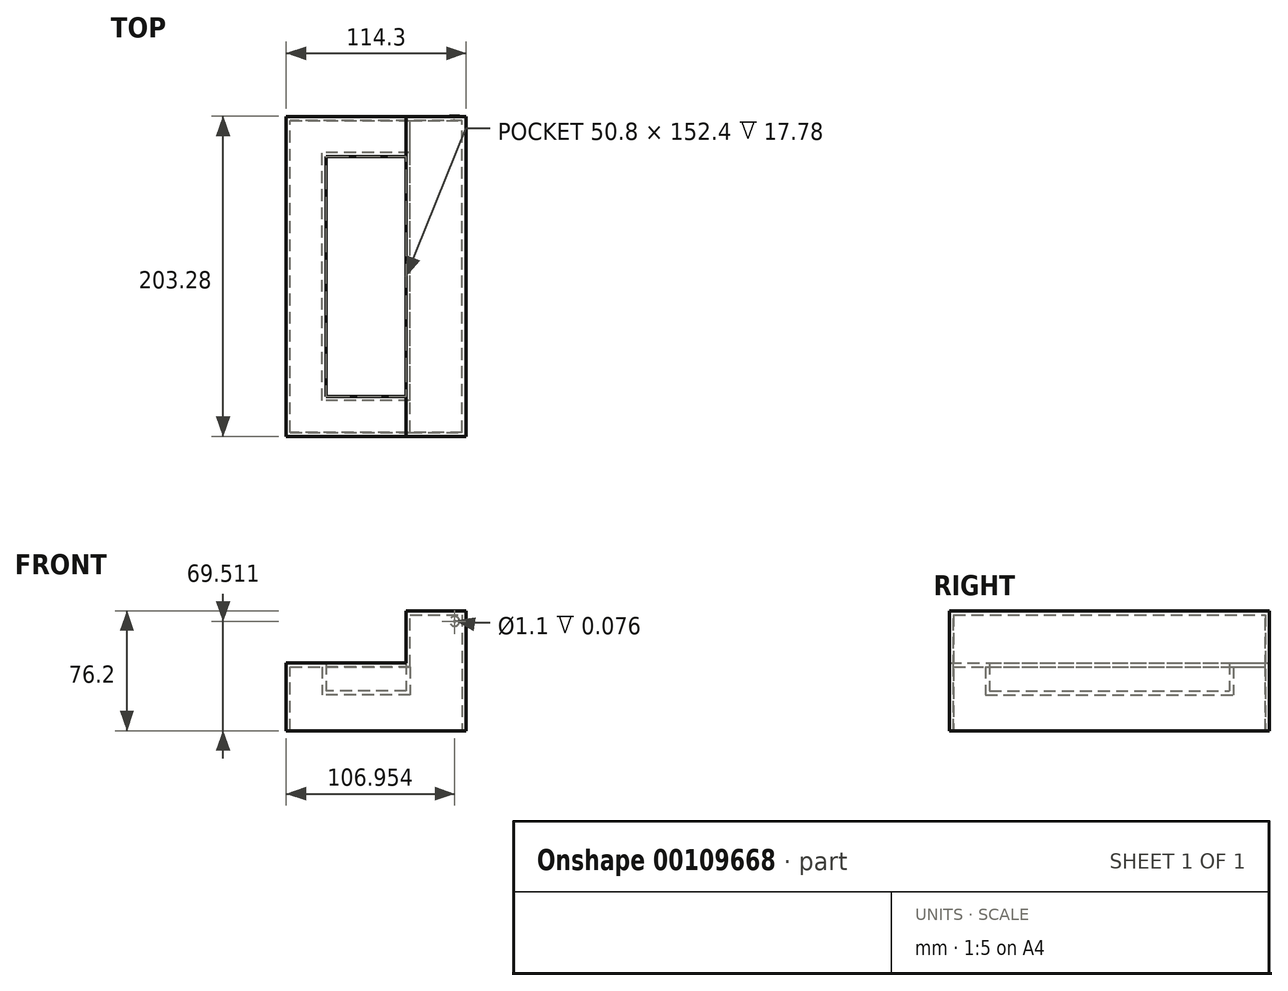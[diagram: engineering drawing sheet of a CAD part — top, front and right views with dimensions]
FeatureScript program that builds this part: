
annotation { "Feature Type Name" : "Feature", "Feature Type Description" : "" }
export const myFeature = defineFeature(function(context is Context, id is Id, definition is map)
    precondition{}
    {
        {
            var Q0;
            Q0=qCreatedBy(makeId("Front.planeOp"),FACE);
            var sketch = newSketch(context, id + "F0", { "sketchPlane" : qUnion([Q0])});
            skLineSegment(sketch, "E0", {"start": v(-17.88, -41.6) * mm, "end": v(7.52, -41.6) * mm});
            skLineSegment(sketch, "E1", {"start": v(7.52, -41.6) * mm, "end": v(7.52, -59.39) * mm});
            skLineSegment(sketch, "E2", {"start": v(7.52, -59.39) * mm, "end": v(58.32, -59.39) * mm});
            skLineSegment(sketch, "E3", {"start": v(58.32, -59.39) * mm, "end": v(58.32, -8.59) * mm});
            skLineSegment(sketch, "E4", {"start": v(58.32, -8.59) * mm, "end": v(96.42, -8.59) * mm});
            skLineSegment(sketch, "E5", {"start": v(96.42, -8.59) * mm, "end": v(96.42, -84.79) * mm});
            skLineSegment(sketch, "E6", {"start": v(96.42, -84.79) * mm, "end": v(-17.88, -84.79) * mm});
            skLineSegment(sketch, "E7", {"start": v(-17.88, -84.79) * mm, "end": v(-17.88, -41.6) * mm});
            skSolve(sketch);
        }
        {
            var Q0;
            Q0=makeQuery(id+"F0.imprint","IMPRINT",FACE,{"disambiguationData":[TD([[makeQuery(id+"F0.imprint","IMPRINT",EDGE,{"derivedFrom":sQuery(id+"F0.wireOp",EDGE,"E0")}),-1.0]])]});
            extrude(context, id + "F1", {"entities" : qUnion([Q0]), "depth" : 203.2 * mm});
        }
        {
            var Q0;
            Q0=makeQuery(id+"F1.opExtrude","SWEPT_FACE",FACE,{"disambiguationData":[OSD([sQuery(id+"F0.wireOp",EDGE,"E1")])]});
            var sketch = newSketch(context, id + "F2", { "sketchPlane" : qUnion([Q0])});
            skLineSegment(sketch, "E8.bottom", {"start": v(-203.2, -41.6) * mm, "end": v(-177.8, -41.6) * mm});
            skLineSegment(sketch, "E8.top", {"start": v(-203.2, -59.39) * mm, "end": v(-177.8, -59.39) * mm});
            skLineSegment(sketch, "E8.left", {"start": v(-203.2, -41.6) * mm, "end": v(-203.2, -59.39) * mm});
            skLineSegment(sketch, "E8.right", {"start": v(-177.8, -41.6) * mm, "end": v(-177.8, -59.39) * mm});
            skSolve(sketch);
        }
        {
            var Q0;
            Q0=makeQuery(id+"F2.imprint","IMPRINT",FACE,{"disambiguationData":[TD([[makeQuery(id+"F2.imprint","IMPRINT",EDGE,{"derivedFrom":sQuery(id+"F2.wireOp",EDGE,"E8.bottom")}),-1.0]])]});
            extrude(context, id + "F3", {"entities" : qUnion([Q0]), "operationType" : NewBodyOperationType.ADD, "depth" : 50.8 * mm});
        }
        {
            var Q0;
            Q0=makeQuery(id+"F1.opExtrude","SWEPT_FACE",FACE,{"disambiguationData":[OSD([sQuery(id+"F0.wireOp",EDGE,"E1")])]});
            var sketch = newSketch(context, id + "F4", { "sketchPlane" : qUnion([Q0])});
            skLineSegment(sketch, "E9.bottom", {"start": v(0, -41.6) * mm, "end": v(-25.4, -41.6) * mm});
            skLineSegment(sketch, "E9.top", {"start": v(0, -59.39) * mm, "end": v(-25.4, -59.39) * mm});
            skLineSegment(sketch, "E9.left", {"start": v(0, -41.6) * mm, "end": v(0, -59.39) * mm});
            skLineSegment(sketch, "E9.right", {"start": v(-25.4, -41.6) * mm, "end": v(-25.4, -59.39) * mm});
            skSolve(sketch);
        }
        {
            var Q0;
            Q0=makeQuery(id+"F4.imprint","IMPRINT",FACE,{"disambiguationData":[TD([[makeQuery(id+"F4.imprint","IMPRINT",EDGE,{"derivedFrom":sQuery(id+"F4.wireOp",EDGE,"E9.bottom")}),-1.0]])]});
            extrude(context, id + "F5", {"entities" : qUnion([Q0]), "operationType" : NewBodyOperationType.ADD, "depth" : 50.8 * mm});
        }
        {
            var Q0;
            Q0=makeQuery(id+"F3.boolean.opBoolean","MERGE",FACE,{"derivedFrom":[makeQuery(id+"F1.opExtrude","CAP_FACE",FACE,{"disambiguationData":[OSD([sQuery(id+"F0.wireOp",EDGE,"E0"),sQuery(id+"F0.wireOp",EDGE,"E1"),sQuery(id+"F0.wireOp",EDGE,"E2"),sQuery(id+"F0.wireOp",EDGE,"E3"),sQuery(id+"F0.wireOp",EDGE,"E4"),sQuery(id+"F0.wireOp",EDGE,"E5"),sQuery(id+"F0.wireOp",EDGE,"E6"),sQuery(id+"F0.wireOp",EDGE,"E7")])],"isStart":false}),makeQuery(id+"F3.opExtrude","SWEPT_FACE",FACE,{"disambiguationData":[OSD([sQuery(id+"F2.wireOp",EDGE,"E8.left")])]})]});
            var sketch = newSketch(context, id + "F6", { "sketchPlane" : qUnion([Q0])});
            skCircle(sketch, "E10", {"center": v(2.53, -60.02) * mm, "radius": 8.97 * mm});
            skCircle(sketch, "E11", {"center": v(2.53, -60.02) * mm, "radius": 6.38 * mm});
            skCircle(sketch, "E12", {"center": v(2.53, -60.02) * mm, "radius": 3.86 * mm});
            skCircle(sketch, "E13", {"center": v(46.1, -54.58) * mm, "radius": 12.1 * mm});
            skCircle(sketch, "E14", {"center": v(46.1, -54.58) * mm, "radius": 8.06 * mm});
            skCircle(sketch, "E15", {"center": v(46.1, -54.58) * mm, "radius": 4.73 * mm});
            skCircle(sketch, "E16", {"center": v(25.1, -66.44) * mm, "radius": 7.01 * mm});
            skCircle(sketch, "E17", {"center": v(25.1, -66.44) * mm, "radius": 5.22 * mm});
            skCircle(sketch, "E18", {"center": v(25.1, -66.44) * mm, "radius": 2.9 * mm});
            skCircle(sketch, "E19", {"center": v(73.33, -30.85) * mm, "radius": 11.18 * mm});
            skCircle(sketch, "E20", {"center": v(73.33, -30.85) * mm, "radius": 8.9 * mm});
            skCircle(sketch, "E21", {"center": v(73.33, -30.85) * mm, "radius": 5.31 * mm});
            skCircle(sketch, "E22", {"center": v(76.83, -56.72) * mm, "radius": 10.12 * mm});
            skCircle(sketch, "E23", {"center": v(76.83, -56.72) * mm, "radius": 6.65 * mm});
            skCircle(sketch, "E24", {"center": v(76.83, -56.72) * mm, "radius": 3.76 * mm});
            skCircle(sketch, "E25", {"center": v(89.09, -15.48) * mm, "radius": 6.23 * mm});
            skCircle(sketch, "E26", {"center": v(89.09, -15.48) * mm, "radius": 4.92 * mm});
            skCircle(sketch, "E27", {"center": v(89.09, -15.48) * mm, "radius": 2.92 * mm});
            skCircle(sketch, "E28", {"center": v(57.58, -75.78) * mm, "radius": 6.65 * mm});
            skCircle(sketch, "E29", {"center": v(57.58, -75.78) * mm, "radius": 4.44 * mm});
            skCircle(sketch, "E30", {"center": v(57.58, -75.78) * mm, "radius": 2.27 * mm});
            skCircle(sketch, "E31", {"center": v(84.8, -75.59) * mm, "radius": 6.4 * mm});
            skCircle(sketch, "E32", {"center": v(84.8, -75.59) * mm, "radius": 4.68 * mm});
            skCircle(sketch, "E33", {"center": v(84.8, -75.59) * mm, "radius": 2.79 * mm});
            skCircle(sketch, "E34", {"center": v(-8.56, -74.8) * mm, "radius": 6.24 * mm});
            skCircle(sketch, "E35", {"center": v(-8.56, -74.8) * mm, "radius": 4.81 * mm});
            skCircle(sketch, "E36", {"center": v(-8.56, -74.8) * mm, "radius": 2.79 * mm});
            skCircle(sketch, "E37", {"center": v(-11.48, -47.19) * mm, "radius": 5.17 * mm});
            skCircle(sketch, "E38", {"center": v(-11.48, -47.19) * mm, "radius": 3.08 * mm});
            skCircle(sketch, "E39", {"center": v(-11.48, -47.19) * mm, "radius": 1.84 * mm});
            skCircle(sketch, "E40", {"center": v(16.92, -50.5) * mm, "radius": 6.14 * mm});
            skCircle(sketch, "E41", {"center": v(16.92, -50.5) * mm, "radius": 4.2 * mm});
            skCircle(sketch, "E42", {"center": v(16.92, -50.5) * mm, "radius": 2.65 * mm});
            skCircle(sketch, "E43", {"center": v(9.72, -76.17) * mm, "radius": 6.72 * mm});
            skCircle(sketch, "E44", {"center": v(9.72, -76.17) * mm, "radius": 5.15 * mm});
            skCircle(sketch, "E45", {"center": v(9.72, -76.17) * mm, "radius": 3.45 * mm});
            skCircle(sketch, "E46", {"center": v(35.98, -76.75) * mm, "radius": 3.02 * mm});
            skCircle(sketch, "E47", {"center": v(35.98, -76.75) * mm, "radius": 1.74 * mm});
            skCircle(sketch, "E48", {"center": v(35.98, -76.75) * mm, "radius": 4.77 * mm});
            skSolve(sketch);
        }
        {
            var Q0;
            Q0=makeQuery(id+"F1.opExtrude","SWEPT_FACE",FACE,{"disambiguationData":[OSD([sQuery(id+"F0.wireOp",EDGE,"E7")])]});
            var sketch = newSketch(context, id + "F7", { "sketchPlane" : qUnion([Q0])});
            skCircle(sketch, "E49", {"center": v(16.84, -58.1) * mm, "radius": 14.47 * mm});
            skCircle(sketch, "E50", {"center": v(16.84, -58.1) * mm, "radius": 9.9 * mm});
            skCircle(sketch, "E51", {"center": v(16.84, -58.1) * mm, "radius": 4.92 * mm});
            skCircle(sketch, "E52", {"center": v(67.39, -64.14) * mm, "radius": 8.57 * mm});
            skCircle(sketch, "E53", {"center": v(67.39, -64.14) * mm, "radius": 4.72 * mm});
            skCircle(sketch, "E54", {"center": v(67.39, -64.14) * mm, "radius": 2.75 * mm});
            skCircle(sketch, "E55", {"center": v(42.18, -76.46) * mm, "radius": 6.39 * mm});
            skCircle(sketch, "E56", {"center": v(42.18, -76.46) * mm, "radius": 4.32 * mm});
            skCircle(sketch, "E57", {"center": v(42.18, -76.46) * mm, "radius": 2.37 * mm});
            skCircle(sketch, "E58", {"center": v(136.66, -60.8) * mm, "radius": 18.27 * mm});
            skCircle(sketch, "E59", {"center": v(136.66, -60.8) * mm, "radius": 13.93 * mm});
            skCircle(sketch, "E60", {"center": v(136.66, -60.8) * mm, "radius": 6.71 * mm});
            skCircle(sketch, "E61", {"center": v(93.8, -50.8) * mm, "radius": 8.12 * mm});
            skCircle(sketch, "E62", {"center": v(93.8, -50.8) * mm, "radius": 5.3 * mm});
            skCircle(sketch, "E63", {"center": v(93.8, -50.8) * mm, "radius": 2.5 * mm});
            skCircle(sketch, "E64", {"center": v(98.58, -69.92) * mm, "radius": 10.13 * mm});
            skCircle(sketch, "E65", {"center": v(98.58, -69.92) * mm, "radius": 6.88 * mm});
            skCircle(sketch, "E66", {"center": v(98.58, -69.92) * mm, "radius": 3.77 * mm});
            skCircle(sketch, "E67", {"center": v(47.63, -54.43) * mm, "radius": 11.32 * mm});
            skCircle(sketch, "E68", {"center": v(47.63, -54.43) * mm, "radius": 7.66 * mm});
            skCircle(sketch, "E69", {"center": v(47.63, -54.43) * mm, "radius": 3.83 * mm});
            skCircle(sketch, "E70", {"center": v(78.4, -78.14) * mm, "radius": 5 * mm});
            skCircle(sketch, "E71", {"center": v(78.4, -78.14) * mm, "radius": 3.43 * mm});
            skCircle(sketch, "E72", {"center": v(78.4, -78.14) * mm, "radius": 1.87 * mm});
            skCircle(sketch, "E73", {"center": v(186.57, -55.2) * mm, "radius": 10.15 * mm});
            skCircle(sketch, "E74", {"center": v(186.57, -55.2) * mm, "radius": 6.62 * mm});
            skCircle(sketch, "E75", {"center": v(186.57, -55.2) * mm, "radius": 3.32 * mm});
            skCircle(sketch, "E76", {"center": v(167.33, -73.7) * mm, "radius": 10.03 * mm});
            skCircle(sketch, "E77", {"center": v(167.33, -73.7) * mm, "radius": 7.44 * mm});
            skCircle(sketch, "E78", {"center": v(167.33, -73.7) * mm, "radius": 3.9 * mm});
            skCircle(sketch, "E79", {"center": v(192.62, -75.94) * mm, "radius": 6.28 * mm});
            skCircle(sketch, "E80", {"center": v(192.62, -75.94) * mm, "radius": 3.83 * mm});
            skCircle(sketch, "E81", {"center": v(192.62, -75.94) * mm, "radius": 1.86 * mm});
            skCircle(sketch, "E82", {"center": v(164.19, -51.52) * mm, "radius": 8.73 * mm});
            skCircle(sketch, "E83", {"center": v(164.19, -51.52) * mm, "radius": 5.7 * mm});
            skCircle(sketch, "E84", {"center": v(164.19, -51.52) * mm, "radius": 3.89 * mm});
            skFitSpline(sketch, "E85", {"points": [v(16.84, -58.1) * mm, v(42.18, -76.46) * mm, v(47.63, -54.43) * mm, v(67.39, -64.14) * mm, v(78.4, -78.14) * mm, v(98.58, -69.92) * mm, v(93.8, -50.8) * mm, v(136.66, -60.8) * mm, v(167.33, -73.7) * mm, v(192.62, -75.94) * mm, v(186.57, -55.2) * mm, v(164.19, -51.52) * mm], "startDerivative": vector(320.34, -333.06) * mm, "endDerivative": vector(-285.34, -29.82) * mm});
            skSolve(sketch);
        }
        {
            var Q0;
            Q0=makeQuery(id+"F1.opExtrude","SWEPT_FACE",FACE,{"disambiguationData":[OSD([sQuery(id+"F0.wireOp",EDGE,"E5")])]});
            var sketch = newSketch(context, id + "F8", { "sketchPlane" : qUnion([Q0])});
            skCircle(sketch, "E86", {"center": v(-102.8, -41.74) * mm, "radius": 32.18 * mm});
            skCircle(sketch, "E87", {"center": v(-134.96, -42.55) * mm, "radius": 4.22 * mm});
            skCircle(sketch, "E88", {"center": v(-102.8, -41.74) * mm, "radius": 24.3 * mm});
            skCircle(sketch, "E89", {"center": v(-102.8, -41.74) * mm, "radius": 18.4 * mm});
            skCircle(sketch, "E90", {"center": v(-102.8, -41.74) * mm, "radius": 11.52 * mm});
            skCircle(sketch, "E91", {"center": v(-102.8, -41.74) * mm, "radius": 5.5 * mm});
            skCircle(sketch, "E92", {"center": v(-95.53, -50.68) * mm, "radius": 1.9 * mm});
            skCircle(sketch, "E93", {"center": v(-91.05, -27.59) * mm, "radius": 3.84 * mm});
            skCircle(sketch, "E94", {"center": v(-115.17, -20.82) * mm, "radius": 3.86 * mm});
            skCircle(sketch, "E95", {"center": v(-188.21, -21.19) * mm, "radius": 12.08 * mm});
            skCircle(sketch, "E96", {"center": v(-181.96, -31.52) * mm, "radius": 5.49 * mm});
            skCircle(sketch, "E97", {"center": v(-160.8, -54.37) * mm, "radius": 12.64 * mm});
            skCircle(sketch, "E98", {"center": v(-173.21, -56.76) * mm, "radius": 6.24 * mm});
            skCircle(sketch, "E99", {"center": v(-149.04, -59) * mm, "radius": 3.57 * mm});
            skCircle(sketch, "E100", {"center": v(-36.12, -36.85) * mm, "radius": 15.12 * mm});
            skCircle(sketch, "E101", {"center": v(-29.87, -23.09) * mm, "radius": 8.62 * mm});
            skCircle(sketch, "E102", {"center": v(-46.01, -14.18) * mm, "radius": 4.2 * mm});
            skCircle(sketch, "E103", {"center": v(-58.79, -71.68) * mm, "radius": 10.96 * mm});
            skCircle(sketch, "E104", {"center": v(-47.66, -73.94) * mm, "radius": 5.98 * mm});
            skCircle(sketch, "E105", {"center": v(-7.06, -77.86) * mm, "radius": 5.5 * mm});
            skCircle(sketch, "E106", {"center": v(-10.27, -73.4) * mm, "radius": 3.76 * mm});
            skCircle(sketch, "E107", {"center": v(-157.71, -21.8) * mm, "radius": 10.15 * mm});
            skCircle(sketch, "E108", {"center": v(-157.71, -21.8) * mm, "radius": 5.1 * mm});
            skCircle(sketch, "E109", {"center": v(-28.08, -65.29) * mm, "radius": 11.15 * mm});
            skCircle(sketch, "E110", {"center": v(-28.08, -64.88) * mm, "radius": 8.5 * mm});
            skCircle(sketch, "E111", {"center": v(-28.08, -64.88) * mm, "radius": 4.25 * mm});
            skCircle(sketch, "E112", {"center": v(-193.36, -74.15) * mm, "radius": 9.03 * mm});
            skCircle(sketch, "E113", {"center": v(-193.36, -74.15) * mm, "radius": 6.97 * mm});
            skCircle(sketch, "E114", {"center": v(-193.36, -74.15) * mm, "radius": 3.72 * mm});
            skCircle(sketch, "E115", {"center": v(-139.16, -75.6) * mm, "radius": 8.32 * mm});
            skCircle(sketch, "E116", {"center": v(-139.16, -75.6) * mm, "radius": 5.57 * mm});
            skCircle(sketch, "E117", {"center": v(-139.16, -75.6) * mm, "radius": 3.6 * mm});
            skCircle(sketch, "E118", {"center": v(-190.68, -51.48) * mm, "radius": 4.12 * mm});
            skCircle(sketch, "E119", {"center": v(-165.34, -75.39) * mm, "radius": 7 * mm});
            skCircle(sketch, "E120", {"center": v(-8.91, -40.35) * mm, "radius": 5.15 * mm});
            skCircle(sketch, "E121", {"center": v(-64.15, -24.48) * mm, "radius": 6.9 * mm});
            skCircle(sketch, "E122", {"center": v(-62.09, -31.08) * mm, "radius": 3.32 * mm});
            skCircle(sketch, "E123", {"center": v(-59.4, -50.04) * mm, "radius": 3.3 * mm});
            skCircle(sketch, "E124", {"center": v(-83.72, -78.9) * mm, "radius": 2.93 * mm});
            skCircle(sketch, "E125", {"center": v(-9.34, -35.22) * mm, "radius": 2.76 * mm});
            skSolve(sketch);
        }
        {
            var Q0;
            Q0=makeQuery(id+"F5.boolean.opBoolean","MERGE",FACE,{"derivedFrom":[makeQuery(id+"F1.opExtrude","CAP_FACE",FACE,{"disambiguationData":[OSD([sQuery(id+"F0.wireOp",EDGE,"E0"),sQuery(id+"F0.wireOp",EDGE,"E1"),sQuery(id+"F0.wireOp",EDGE,"E2"),sQuery(id+"F0.wireOp",EDGE,"E3"),sQuery(id+"F0.wireOp",EDGE,"E4"),sQuery(id+"F0.wireOp",EDGE,"E5"),sQuery(id+"F0.wireOp",EDGE,"E6"),sQuery(id+"F0.wireOp",EDGE,"E7")])],"isStart":true}),makeQuery(id+"F5.opExtrude","SWEPT_FACE",FACE,{"disambiguationData":[OSD([sQuery(id+"F4.wireOp",EDGE,"E9.left")])]})]});
            var sketch = newSketch(context, id + "F9", { "sketchPlane" : qUnion([Q0])});
            skCircle(sketch, "E126", {"center": v(-73.48, -30.87) * mm, "radius": 5.53 * mm});
            skCircle(sketch, "E127", {"center": v(-73.48, -30.87) * mm, "radius": 9.24 * mm});
            skCircle(sketch, "E128", {"center": v(-73.48, -30.87) * mm, "radius": 11.46 * mm});
            skCircle(sketch, "E129", {"center": v(-89.07, -15.28) * mm, "radius": 3.09 * mm});
            skCircle(sketch, "E130", {"center": v(-89.07, -15.28) * mm, "radius": 4.64 * mm});
            skCircle(sketch, "E131", {"center": v(-89.07, -15.28) * mm, "radius": 6.15 * mm});
            skCircle(sketch, "E132", {"center": v(-77.19, -56.81) * mm, "radius": 3.84 * mm});
            skCircle(sketch, "E133", {"center": v(-77.19, -56.81) * mm, "radius": 6.8 * mm});
            skCircle(sketch, "E134", {"center": v(-77.19, -56.81) * mm, "radius": 10.29 * mm});
            skCircle(sketch, "E135", {"center": v(-84.75, -75.5) * mm, "radius": 2.44 * mm});
            skCircle(sketch, "E136", {"center": v(-84.75, -75.5) * mm, "radius": 4.77 * mm});
            skCircle(sketch, "E137", {"center": v(-84.75, -75.5) * mm, "radius": 6.56 * mm});
            skCircle(sketch, "E138", {"center": v(-46.15, -54.34) * mm, "radius": 4.88 * mm});
            skCircle(sketch, "E139", {"center": v(-46.15, -54.34) * mm, "radius": 7.97 * mm});
            skCircle(sketch, "E140", {"center": v(-46.15, -54.34) * mm, "radius": 12.01 * mm});
            skCircle(sketch, "E141", {"center": v(-57.11, -75.65) * mm, "radius": 2.57 * mm});
            skCircle(sketch, "E142", {"center": v(-57.11, -75.65) * mm, "radius": 3.87 * mm});
            skCircle(sketch, "E143", {"center": v(-57.11, -75.65) * mm, "radius": 6.47 * mm});
            skCircle(sketch, "E144", {"center": v(-36.12, -76.57) * mm, "radius": 1.64 * mm});
            skCircle(sketch, "E145", {"center": v(-36.12, -76.57) * mm, "radius": 3.13 * mm});
            skCircle(sketch, "E146", {"center": v(-36.12, -76.57) * mm, "radius": 5.02 * mm});
            skCircle(sketch, "E147", {"center": v(-25.16, -66.54) * mm, "radius": 7.18 * mm});
            skCircle(sketch, "E148", {"center": v(-25.16, -66.54) * mm, "radius": 5.22 * mm});
            skCircle(sketch, "E149", {"center": v(-25.16, -66.54) * mm, "radius": 3.05 * mm});
            skCircle(sketch, "E150", {"center": v(-16.97, -50.17) * mm, "radius": 6.18 * mm});
            skCircle(sketch, "E151", {"center": v(-16.97, -50.17) * mm, "radius": 4 * mm});
            skCircle(sketch, "E152", {"center": v(-16.97, -50.17) * mm, "radius": 2.74 * mm});
            skCircle(sketch, "E153", {"center": v(11.44, -46.62) * mm, "radius": 1.95 * mm});
            skCircle(sketch, "E154", {"center": v(11.44, -46.62) * mm, "radius": 3.45 * mm});
            skCircle(sketch, "E155", {"center": v(11.44, -46.62) * mm, "radius": 4.74 * mm});
            skCircle(sketch, "E156", {"center": v(-9.87, -75.8) * mm, "radius": 2 * mm});
            skCircle(sketch, "E157", {"center": v(-9.87, -75.8) * mm, "radius": 4.54 * mm});
            skCircle(sketch, "E158", {"center": v(-9.87, -75.8) * mm, "radius": 6.42 * mm});
            skCircle(sketch, "E159", {"center": v(8.35, -74.72) * mm, "radius": 2.57 * mm});
            skCircle(sketch, "E160", {"center": v(8.81, -74.41) * mm, "radius": 5.11 * mm});
            skCircle(sketch, "E161", {"center": v(8.81, -74.41) * mm, "radius": 6.63 * mm});
            skCircle(sketch, "E162", {"center": v(-2.46, -60.36) * mm, "radius": 4.08 * mm});
            skCircle(sketch, "E163", {"center": v(-2.46, -60.36) * mm, "radius": 6.63 * mm});
            skCircle(sketch, "E164", {"center": v(-2.46, -60.36) * mm, "radius": 8.11 * mm});
            skFitSpline(sketch, "E165", {"points": [v(-89.07, -15.28) * mm, v(-73.48, -30.87) * mm, v(-77.19, -56.81) * mm, v(-84.75, -75.5) * mm, v(-57.11, -75.65) * mm, v(-46.15, -54.34) * mm, v(-36.12, -76.57) * mm, v(-25.16, -66.54) * mm, v(-9.87, -75.8) * mm, v(8.35, -74.72) * mm, v(-2.46, -60.36) * mm, v(11.44, -46.62) * mm, v(-16.97, -50.17) * mm], "startDerivative": vector(231.64, -158.41) * mm, "endDerivative": vector(-467.12, -94.84) * mm});
            skSolve(sketch);
        }
        {
            var Q0;
            Q0=sQuery(id+"F9.wireOp",EDGE,"E131");
            var Q1;
            Q1=sQuery(id+"F9.wireOp",EDGE,"E128");
            var Q2;
            Q2=sQuery(id+"F9.wireOp",EDGE,"E134");
            var Q3;
            Q3=sQuery(id+"F9.wireOp",EDGE,"E137");
            var Q4;
            Q4=sQuery(id+"F6.wireOp",EDGE,"E28");
            var Q5;
            Q5=sQuery(id+"F6.wireOp",EDGE,"E13");
            var Q6;
            Q6=sQuery(id+"F9.wireOp",EDGE,"E146");
            var Q7;
            Q7=sQuery(id+"F6.wireOp",EDGE,"E16");
            var Q8;
            Q8=sQuery(id+"F6.wireOp",EDGE,"E40");
            var Q9;
            Q9=sQuery(id+"F6.wireOp",EDGE,"E37");
            var Q10;
            Q10=sQuery(id+"F6.wireOp",EDGE,"E10");
            var Q11;
            Q11=sQuery(id+"F6.wireOp",EDGE,"E43");
            var Q12;
            Q12=sQuery(id+"F9.wireOp",EDGE,"E161");
            extrude(context, id + "F10", {"bodyType" : ToolBodyType.SURFACE, "surfaceEntities" : qUnion([Q0, Q1, Q2, Q3, Q4, Q5, Q6, Q7, Q8, Q9, Q10, Q11, Q12]), "depth" : 0.05 * mm});
        }
        {
            var Q0;
            Q0=makeQuery(id+"F9.imprint","IMPRINT",FACE,{"disambiguationData":[TD([[makeQuery(id+"F9.imprint","IMPRINT",EDGE,{"derivedFrom":sQuery(id+"F9.wireOp",EDGE,"E129")}),1.0]])]});
            extrude(context, id + "F11", {"entities" : qUnion([Q0]), "operationType" : NewBodyOperationType.ADD, "depth" : 0.08 * mm});
        }
        {
            var Q0;
            Q0=sQuery(id+"F9.wireOp",EDGE,"E128");
            var Q1;
            Q1=sQuery(id+"F9.wireOp",EDGE,"E134");
            var Q2;
            Q2=sQuery(id+"F9.wireOp",EDGE,"E137");
            var Q3;
            Q3=sQuery(id+"F9.wireOp",EDGE,"E140");
            var Q4;
            Q4=sQuery(id+"F9.wireOp",EDGE,"E143");
            var Q5;
            Q5=sQuery(id+"F9.wireOp",EDGE,"E146");
            var Q6;
            Q6=sQuery(id+"F9.wireOp",EDGE,"E147");
            var Q7;
            Q7=sQuery(id+"F9.wireOp",EDGE,"E150");
            var Q8;
            Q8=sQuery(id+"F9.wireOp",EDGE,"E155");
            var Q9;
            Q9=sQuery(id+"F9.wireOp",EDGE,"E164");
            var Q10;
            Q10=sQuery(id+"F9.wireOp",EDGE,"E158");
            var Q11;
            Q11=sQuery(id+"F9.wireOp",EDGE,"E161");
            extrude(context, id + "F12", {"bodyType" : ToolBodyType.SURFACE, "surfaceEntities" : qUnion([Q0, Q1, Q2, Q3, Q4, Q5, Q6, Q7, Q8, Q9, Q10, Q11]), "depth" : 0.05 * mm});
        }
        {
            var Q0;
            Q0=sQuery(id+"F9.wireOp",EDGE,"E127");
            var Q1;
            Q1=sQuery(id+"F9.wireOp",EDGE,"E133");
            var Q2;
            Q2=sQuery(id+"F9.wireOp",EDGE,"E136");
            var Q3;
            Q3=sQuery(id+"F9.wireOp",EDGE,"E139");
            var Q4;
            Q4=sQuery(id+"F9.wireOp",EDGE,"E142");
            var Q5;
            Q5=sQuery(id+"F9.wireOp",EDGE,"E145");
            var Q6;
            Q6=sQuery(id+"F9.wireOp",EDGE,"E148");
            var Q7;
            Q7=sQuery(id+"F9.wireOp",EDGE,"E151");
            var Q8;
            Q8=sQuery(id+"F9.wireOp",EDGE,"E154");
            var Q9;
            Q9=sQuery(id+"F9.wireOp",EDGE,"E163");
            var Q10;
            Q10=sQuery(id+"F9.wireOp",EDGE,"E157");
            var Q11;
            Q11=sQuery(id+"F9.wireOp",EDGE,"E160");
            extrude(context, id + "F13", {"bodyType" : ToolBodyType.SURFACE, "surfaceEntities" : qUnion([Q0, Q1, Q2, Q3, Q4, Q5, Q6, Q7, Q8, Q9, Q10, Q11]), "depth" : 0.08 * mm});
        }
        {
            var Q0;
            Q0=sQuery(id+"F9.wireOp",EDGE,"E129");
            var Q1;
            Q1=sQuery(id+"F9.wireOp",EDGE,"E126");
            var Q2;
            Q2=sQuery(id+"F9.wireOp",EDGE,"E132");
            var Q3;
            Q3=sQuery(id+"F9.wireOp",EDGE,"E135");
            var Q4;
            Q4=sQuery(id+"F9.wireOp",EDGE,"E138");
            var Q5;
            Q5=sQuery(id+"F9.wireOp",EDGE,"E141");
            var Q6;
            Q6=sQuery(id+"F9.wireOp",EDGE,"E144");
            var Q7;
            Q7=sQuery(id+"F9.wireOp",EDGE,"E149");
            var Q8;
            Q8=sQuery(id+"F9.wireOp",EDGE,"E152");
            var Q9;
            Q9=sQuery(id+"F9.wireOp",EDGE,"E162");
            var Q10;
            Q10=sQuery(id+"F9.wireOp",EDGE,"E153");
            var Q11;
            Q11=sQuery(id+"F9.wireOp",EDGE,"E156");
            var Q12;
            Q12=sQuery(id+"F9.wireOp",EDGE,"E159");
            extrude(context, id + "F14", {"bodyType" : ToolBodyType.SURFACE, "surfaceEntities" : qUnion([Q0, Q1, Q2, Q3, Q4, Q5, Q6, Q7, Q8, Q9, Q10, Q11, Q12]), "depth" : 0.1 * mm});
        }
        {
            var Q0;
            Q0=sQuery(id+"F7.wireOp",EDGE,"E49");
            var Q1;
            Q1=sQuery(id+"F7.wireOp",EDGE,"E67");
            var Q2;
            Q2=sQuery(id+"F7.wireOp",EDGE,"E55");
            var Q3;
            Q3=sQuery(id+"F7.wireOp",EDGE,"E52");
            var Q4;
            Q4=sQuery(id+"F7.wireOp",EDGE,"E70");
            var Q5;
            Q5=sQuery(id+"F7.wireOp",EDGE,"E64");
            var Q6;
            Q6=sQuery(id+"F7.wireOp",EDGE,"E61");
            var Q7;
            Q7=sQuery(id+"F7.wireOp",EDGE,"E58");
            var Q8;
            Q8=sQuery(id+"F7.wireOp",EDGE,"E76");
            var Q9;
            Q9=sQuery(id+"F7.wireOp",EDGE,"E82");
            var Q10;
            Q10=sQuery(id+"F7.wireOp",EDGE,"E73");
            var Q11;
            Q11=sQuery(id+"F7.wireOp",EDGE,"E79");
            extrude(context, id + "F15", {"bodyType" : ToolBodyType.SURFACE, "surfaceEntities" : qUnion([Q0, Q1, Q2, Q3, Q4, Q5, Q6, Q7, Q8, Q9, Q10, Q11]), "depth" : 0.05 * mm});
        }
        {
            var Q0;
            Q0=sQuery(id+"F7.wireOp",EDGE,"E50");
            var Q1;
            Q1=sQuery(id+"F7.wireOp",EDGE,"E68");
            var Q2;
            Q2=sQuery(id+"F7.wireOp",EDGE,"E56");
            var Q3;
            Q3=sQuery(id+"F7.wireOp",EDGE,"E53");
            var Q4;
            Q4=sQuery(id+"F7.wireOp",EDGE,"E71");
            var Q5;
            Q5=sQuery(id+"F7.wireOp",EDGE,"E62");
            var Q6;
            Q6=sQuery(id+"F7.wireOp",EDGE,"E65");
            var Q7;
            Q7=sQuery(id+"F7.wireOp",EDGE,"E59");
            var Q8;
            Q8=sQuery(id+"F7.wireOp",EDGE,"E83");
            var Q9;
            Q9=sQuery(id+"F7.wireOp",EDGE,"E74");
            var Q10;
            Q10=sQuery(id+"F7.wireOp",EDGE,"E80");
            var Q11;
            Q11=sQuery(id+"F7.wireOp",EDGE,"E77");
            extrude(context, id + "F16", {"bodyType" : ToolBodyType.SURFACE, "surfaceEntities" : qUnion([Q0, Q1, Q2, Q3, Q4, Q5, Q6, Q7, Q8, Q9, Q10, Q11]), "depth" : 0.08 * mm});
        }
        {
            var Q0;
            Q0=sQuery(id+"F7.wireOp",EDGE,"E51");
            var Q1;
            Q1=sQuery(id+"F7.wireOp",EDGE,"E57");
            var Q2;
            Q2=sQuery(id+"F7.wireOp",EDGE,"E69");
            var Q3;
            Q3=sQuery(id+"F7.wireOp",EDGE,"E54");
            var Q4;
            Q4=sQuery(id+"F7.wireOp",EDGE,"E72");
            var Q5;
            Q5=sQuery(id+"F7.wireOp",EDGE,"E66");
            var Q6;
            Q6=sQuery(id+"F7.wireOp",EDGE,"E63");
            var Q7;
            Q7=sQuery(id+"F7.wireOp",EDGE,"E60");
            var Q8;
            Q8=sQuery(id+"F7.wireOp",EDGE,"E84");
            var Q9;
            Q9=sQuery(id+"F7.wireOp",EDGE,"E75");
            var Q10;
            Q10=sQuery(id+"F7.wireOp",EDGE,"E81");
            var Q11;
            Q11=sQuery(id+"F7.wireOp",EDGE,"E78");
            extrude(context, id + "F17", {"bodyType" : ToolBodyType.SURFACE, "surfaceEntities" : qUnion([Q0, Q1, Q2, Q3, Q4, Q5, Q6, Q7, Q8, Q9, Q10, Q11]), "depth" : 0.1 * mm});
        }
        {
            var Q0;
            Q0=sQuery(id+"F8.wireOp",EDGE,"E100");
            var Q1;
            Q1=sQuery(id+"F8.wireOp",EDGE,"E121");
            var Q2;
            Q2=sQuery(id+"F8.wireOp",EDGE,"E120");
            var Q3;
            Q3=sQuery(id+"F8.wireOp",EDGE,"E105");
            var Q4;
            Q4=sQuery(id+"F8.wireOp",EDGE,"E103");
            var Q5;
            Q5=sQuery(id+"F8.wireOp",EDGE,"E97");
            var Q6;
            Q6=sQuery(id+"F8.wireOp",EDGE,"E95");
            var Q7;
            Q7=sQuery(id+"F8.wireOp",EDGE,"E90");
            var Q8;
            Q8=sQuery(id+"F8.wireOp",EDGE,"E89");
            var Q9;
            Q9=sQuery(id+"F8.wireOp",EDGE,"E88");
            var Q10;
            Q10=sQuery(id+"F8.wireOp",EDGE,"E86");
            extrude(context, id + "F18", {"bodyType" : ToolBodyType.SURFACE, "surfaceEntities" : qUnion([Q0, Q1, Q2, Q3, Q4, Q5, Q6, Q7, Q8, Q9, Q10]), "depth" : 0.05 * mm});
        }
        {
            var Q0;
            Q0=sQuery(id+"F8.wireOp",EDGE,"E96");
            var Q1;
            Q1=sQuery(id+"F8.wireOp",EDGE,"E87");
            var Q2;
            Q2=sQuery(id+"F8.wireOp",EDGE,"E94");
            var Q3;
            Q3=sQuery(id+"F8.wireOp",EDGE,"E93");
            var Q4;
            Q4=sQuery(id+"F8.wireOp",EDGE,"E92");
            var Q5;
            Q5=sQuery(id+"F8.wireOp",EDGE,"E122");
            var Q6;
            Q6=sQuery(id+"F8.wireOp",EDGE,"E101");
            var Q7;
            Q7=sQuery(id+"F8.wireOp",EDGE,"E125");
            var Q8;
            Q8=sQuery(id+"F8.wireOp",EDGE,"E106");
            var Q9;
            Q9=sQuery(id+"F8.wireOp",EDGE,"E104");
            var Q10;
            Q10=sQuery(id+"F8.wireOp",EDGE,"E98");
            var Q11;
            Q11=sQuery(id+"F8.wireOp",EDGE,"E99");
            extrude(context, id + "F19", {"bodyType" : ToolBodyType.SURFACE, "surfaceEntities" : qUnion([Q0, Q1, Q2, Q3, Q4, Q5, Q6, Q7, Q8, Q9, Q10, Q11]), "depth" : 0.08 * mm});
        }
        {
            var Q0;
            Q0=sQuery(id+"F8.wireOp",EDGE,"E114");
            var Q1;
            Q1=sQuery(id+"F8.wireOp",EDGE,"E91");
            var Q2;
            Q2=sQuery(id+"F8.wireOp",EDGE,"E117");
            var Q3;
            Q3=sQuery(id+"F8.wireOp",EDGE,"E119");
            var Q4;
            Q4=sQuery(id+"F8.wireOp",EDGE,"E118");
            var Q5;
            Q5=sQuery(id+"F8.wireOp",EDGE,"E108");
            var Q6;
            Q6=sQuery(id+"F8.wireOp",EDGE,"E102");
            var Q7;
            Q7=sQuery(id+"F8.wireOp",EDGE,"E123");
            var Q8;
            Q8=sQuery(id+"F8.wireOp",EDGE,"E124");
            var Q9;
            Q9=sQuery(id+"F8.wireOp",EDGE,"E111");
            extrude(context, id + "F20", {"bodyType" : ToolBodyType.SURFACE, "surfaceEntities" : qUnion([Q0, Q1, Q2, Q3, Q4, Q5, Q6, Q7, Q8, Q9]), "depth" : 0.05 * mm});
        }
        {
            var Q0;
            Q0=sQuery(id+"F8.wireOp",EDGE,"E113");
            var Q1;
            Q1=sQuery(id+"F8.wireOp",EDGE,"E116");
            var Q2;
            Q2=sQuery(id+"F8.wireOp",EDGE,"E110");
            var Q3;
            Q3=sQuery(id+"F8.wireOp",EDGE,"E107");
            extrude(context, id + "F21", {"bodyType" : ToolBodyType.SURFACE, "surfaceEntities" : qUnion([Q0, Q1, Q2, Q3]), "depth" : 0.08 * mm});
        }
        {
            var Q0;
            Q0=sQuery(id+"F8.wireOp",EDGE,"E112");
            var Q1;
            Q1=sQuery(id+"F8.wireOp",EDGE,"E115");
            var Q2;
            Q2=sQuery(id+"F8.wireOp",EDGE,"E109");
            extrude(context, id + "F22", {"bodyType" : ToolBodyType.SURFACE, "surfaceEntities" : qUnion([Q0, Q1, Q2]), "depth" : 0.1 * mm});
        }
        {
            var Q0;
            Q0=sQuery(id+"F6.wireOp",EDGE,"E25");
            var Q1;
            Q1=sQuery(id+"F6.wireOp",EDGE,"E19");
            var Q2;
            Q2=sQuery(id+"F6.wireOp",EDGE,"E22");
            var Q3;
            Q3=sQuery(id+"F6.wireOp",EDGE,"E31");
            var Q4;
            Q4=sQuery(id+"F6.wireOp",EDGE,"E28");
            extrude(context, id + "F23", {"bodyType" : ToolBodyType.SURFACE, "surfaceEntities" : qUnion([Q0, Q1, Q2, Q3, Q4]), "depth" : 0.05 * mm});
        }
        {
            var Q0;
            Q0=sQuery(id+"F6.wireOp",EDGE,"E26");
            var Q1;
            Q1=sQuery(id+"F6.wireOp",EDGE,"E20");
            var Q2;
            Q2=sQuery(id+"F6.wireOp",EDGE,"E23");
            var Q3;
            Q3=sQuery(id+"F6.wireOp",EDGE,"E32");
            var Q4;
            Q4=sQuery(id+"F6.wireOp",EDGE,"E29");
            var Q5;
            Q5=sQuery(id+"F6.wireOp",EDGE,"E14");
            var Q6;
            Q6=sQuery(id+"F6.wireOp",EDGE,"E46");
            var Q7;
            Q7=sQuery(id+"F6.wireOp",EDGE,"E17");
            var Q8;
            Q8=sQuery(id+"F6.wireOp",EDGE,"E41");
            var Q9;
            Q9=sQuery(id+"F6.wireOp",EDGE,"E11");
            var Q10;
            Q10=sQuery(id+"F6.wireOp",EDGE,"E44");
            var Q11;
            Q11=sQuery(id+"F6.wireOp",EDGE,"E35");
            var Q12;
            Q12=sQuery(id+"F6.wireOp",EDGE,"E38");
            extrude(context, id + "F24", {"bodyType" : ToolBodyType.SURFACE, "surfaceEntities" : qUnion([Q0, Q1, Q2, Q3, Q4, Q5, Q6, Q7, Q8, Q9, Q10, Q11, Q12]), "depth" : 0.08 * mm});
        }
        {
            var Q0;
            Q0=sQuery(id+"F6.wireOp",EDGE,"E27");
            var Q1;
            Q1=sQuery(id+"F6.wireOp",EDGE,"E21");
            var Q2;
            Q2=sQuery(id+"F6.wireOp",EDGE,"E24");
            var Q3;
            Q3=sQuery(id+"F6.wireOp",EDGE,"E33");
            var Q4;
            Q4=sQuery(id+"F6.wireOp",EDGE,"E30");
            var Q5;
            Q5=sQuery(id+"F6.wireOp",EDGE,"E15");
            var Q6;
            Q6=sQuery(id+"F6.wireOp",EDGE,"E47");
            var Q7;
            Q7=sQuery(id+"F6.wireOp",EDGE,"E18");
            var Q8;
            Q8=sQuery(id+"F6.wireOp",EDGE,"E42");
            var Q9;
            Q9=sQuery(id+"F6.wireOp",EDGE,"E12");
            var Q10;
            Q10=sQuery(id+"F6.wireOp",EDGE,"E39");
            var Q11;
            Q11=sQuery(id+"F6.wireOp",EDGE,"E45");
            var Q12;
            Q12=sQuery(id+"F6.wireOp",EDGE,"E36");
            extrude(context, id + "F25", {"bodyType" : ToolBodyType.SURFACE, "surfaceEntities" : qUnion([Q0, Q1, Q2, Q3, Q4, Q5, Q6, Q7, Q8, Q9, Q10, Q11, Q12]), "depth" : 0.1 * mm});
        }
        {
            var Q0;
            Q0=sQuery(id+"F6.wireOp",EDGE,"E48");
            var Q1;
            Q1=sQuery(id+"F6.wireOp",EDGE,"E34");
            extrude(context, id + "F26", {"bodyType" : ToolBodyType.SURFACE, "surfaceEntities" : qUnion([Q0, Q1]), "depth" : 0.05 * mm});
        }
        {
            var Q0;
            Q0=makeQuery(id+"F1.opExtrude","SWEPT_FACE",FACE,{"disambiguationData":[OSD([sQuery(id+"F0.wireOp",EDGE,"E4")])]});
            var sketch = newSketch(context, id + "F27", { "sketchPlane" : qUnion([Q0])});
            skCircle(sketch, "E166", {"center": v(86.94, -88.7) * mm, "radius": 7.06 * mm});
            skCircle(sketch, "E167", {"center": v(82.24, -19.15) * mm, "radius": 13.66 * mm});
            skCircle(sketch, "E168", {"center": v(82.24, -19.15) * mm, "radius": 7.93 * mm});
            skCircle(sketch, "E169", {"center": v(82.24, -19.15) * mm, "radius": 4.48 * mm});
            skCircle(sketch, "E170", {"center": v(70.81, -50.62) * mm, "radius": 11.61 * mm});
            skCircle(sketch, "E171", {"center": v(70.81, -50.62) * mm, "radius": 8.25 * mm});
            skCircle(sketch, "E172", {"center": v(70.81, -50.62) * mm, "radius": 4.16 * mm});
            skCircle(sketch, "E173", {"center": v(86.94, -88.7) * mm, "radius": 4.86 * mm});
            skCircle(sketch, "E174", {"center": v(86.94, -88.7) * mm, "radius": 2.59 * mm});
            skCircle(sketch, "E175", {"center": v(73.55, -111.47) * mm, "radius": 10.65 * mm});
            skCircle(sketch, "E176", {"center": v(73.55, -111.47) * mm, "radius": 6.88 * mm});
            skCircle(sketch, "E177", {"center": v(73.55, -111.47) * mm, "radius": 3.8 * mm});
            skCircle(sketch, "E178", {"center": v(72.02, -77.9) * mm, "radius": 4 * mm});
            skCircle(sketch, "E179", {"center": v(72.02, -77.9) * mm, "radius": 3.17 * mm});
            skCircle(sketch, "E180", {"center": v(72.02, -77.9) * mm, "radius": 1.84 * mm});
            skCircle(sketch, "E181", {"center": v(64.84, -26.11) * mm, "radius": 4.02 * mm});
            skCircle(sketch, "E182", {"center": v(64.84, -26.11) * mm, "radius": 3.06 * mm});
            skCircle(sketch, "E183", {"center": v(64.84, -26.11) * mm, "radius": 1.62 * mm});
            skCircle(sketch, "E184", {"center": v(87.43, -62.89) * mm, "radius": 6.98 * mm});
            skCircle(sketch, "E185", {"center": v(87.43, -62.89) * mm, "radius": 4.99 * mm});
            skCircle(sketch, "E186", {"center": v(87.43, -62.89) * mm, "radius": 2.71 * mm});
            skCircle(sketch, "E187", {"center": v(68.02, -90.55) * mm, "radius": 6.63 * mm});
            skCircle(sketch, "E188", {"center": v(68.02, -90.55) * mm, "radius": 4.85 * mm});
            skCircle(sketch, "E189", {"center": v(68.02, -90.55) * mm, "radius": 3.07 * mm});
            skCircle(sketch, "E190", {"center": v(79.07, -146.77) * mm, "radius": 15.57 * mm});
            skCircle(sketch, "E191", {"center": v(79.07, -146.77) * mm, "radius": 12.43 * mm});
            skCircle(sketch, "E192", {"center": v(79.07, -146.77) * mm, "radius": 7.53 * mm});
            skCircle(sketch, "E193", {"center": v(84.6, -182.24) * mm, "radius": 7.54 * mm});
            skCircle(sketch, "E194", {"center": v(84.6, -182.24) * mm, "radius": 4.3 * mm});
            skCircle(sketch, "E195", {"center": v(84.6, -182.24) * mm, "radius": 1.98 * mm});
            skCircle(sketch, "E196", {"center": v(66.37, -192.46) * mm, "radius": 5.94 * mm});
            skCircle(sketch, "E197", {"center": v(66.37, -192.46) * mm, "radius": 4.13 * mm});
            skCircle(sketch, "E198", {"center": v(66.37, -192.46) * mm, "radius": 2.56 * mm});
            skCircle(sketch, "E199", {"center": v(67.28, -170.88) * mm, "radius": 8.04 * mm});
            skCircle(sketch, "E200", {"center": v(67.28, -170.88) * mm, "radius": 4.57 * mm});
            skCircle(sketch, "E201", {"center": v(67.28, -170.88) * mm, "radius": 1.98 * mm});
            skSolve(sketch);
        }
        {
            var Q0;
            Q0=sQuery(id+"F27.wireOp",EDGE,"E167");
            var Q1;
            Q1=sQuery(id+"F27.wireOp",EDGE,"E181");
            var Q2;
            Q2=sQuery(id+"F27.wireOp",EDGE,"E170");
            var Q3;
            Q3=sQuery(id+"F27.wireOp",EDGE,"E184");
            var Q4;
            Q4=sQuery(id+"F27.wireOp",EDGE,"E166");
            var Q5;
            Q5=sQuery(id+"F27.wireOp",EDGE,"E178");
            var Q6;
            Q6=sQuery(id+"F27.wireOp",EDGE,"E187");
            var Q7;
            Q7=sQuery(id+"F27.wireOp",EDGE,"E175");
            var Q8;
            Q8=sQuery(id+"F27.wireOp",EDGE,"E190");
            var Q9;
            Q9=sQuery(id+"F27.wireOp",EDGE,"E193");
            var Q10;
            Q10=sQuery(id+"F27.wireOp",EDGE,"E199");
            var Q11;
            Q11=sQuery(id+"F27.wireOp",EDGE,"E196");
            extrude(context, id + "F28", {"bodyType" : ToolBodyType.SURFACE, "surfaceEntities" : qUnion([Q0, Q1, Q2, Q3, Q4, Q5, Q6, Q7, Q8, Q9, Q10, Q11]), "depth" : 0.05 * mm});
        }
        {
            var Q0;
            Q0=sQuery(id+"F27.wireOp",EDGE,"E168");
            var Q1;
            Q1=sQuery(id+"F27.wireOp",EDGE,"E182");
            var Q2;
            Q2=sQuery(id+"F27.wireOp",EDGE,"E171");
            var Q3;
            Q3=sQuery(id+"F27.wireOp",EDGE,"E185");
            var Q4;
            Q4=sQuery(id+"F27.wireOp",EDGE,"E173");
            var Q5;
            Q5=sQuery(id+"F27.wireOp",EDGE,"E179");
            var Q6;
            Q6=sQuery(id+"F27.wireOp",EDGE,"E188");
            var Q7;
            Q7=sQuery(id+"F27.wireOp",EDGE,"E176");
            var Q8;
            Q8=sQuery(id+"F27.wireOp",EDGE,"E191");
            var Q9;
            Q9=sQuery(id+"F27.wireOp",EDGE,"E200");
            var Q10;
            Q10=sQuery(id+"F27.wireOp",EDGE,"E194");
            var Q11;
            Q11=sQuery(id+"F27.wireOp",EDGE,"E197");
            extrude(context, id + "F29", {"bodyType" : ToolBodyType.SURFACE, "surfaceEntities" : qUnion([Q0, Q1, Q2, Q3, Q4, Q5, Q6, Q7, Q8, Q9, Q10, Q11]), "depth" : 0.08 * mm});
        }
        {
            var Q0;
            Q0=sQuery(id+"F27.wireOp",EDGE,"E169");
            var Q1;
            Q1=sQuery(id+"F27.wireOp",EDGE,"E183");
            var Q2;
            Q2=sQuery(id+"F27.wireOp",EDGE,"E172");
            var Q3;
            Q3=sQuery(id+"F27.wireOp",EDGE,"E186");
            var Q4;
            Q4=sQuery(id+"F27.wireOp",EDGE,"E174");
            var Q5;
            Q5=sQuery(id+"F27.wireOp",EDGE,"E180");
            var Q6;
            Q6=sQuery(id+"F27.wireOp",EDGE,"E189");
            var Q7;
            Q7=sQuery(id+"F27.wireOp",EDGE,"E177");
            var Q8;
            Q8=sQuery(id+"F27.wireOp",EDGE,"E192");
            var Q9;
            Q9=sQuery(id+"F27.wireOp",EDGE,"E201");
            var Q10;
            Q10=sQuery(id+"F27.wireOp",EDGE,"E195");
            var Q11;
            Q11=sQuery(id+"F27.wireOp",EDGE,"E198");
            extrude(context, id + "F30", {"bodyType" : ToolBodyType.SURFACE, "surfaceEntities" : qUnion([Q0, Q1, Q2, Q3, Q4, Q5, Q6, Q7, Q8, Q9, Q10, Q11]), "depth" : 0.1 * mm});
        }
        {
            var Q0;
            Q0=makeQuery(id+"F1.opExtrude","SWEPT_FACE",FACE,{"disambiguationData":[OSD([sQuery(id+"F0.wireOp",EDGE,"E6")])]});
            shell(context, id + "F31", {"entities" : qUnion([Q0]), "thickness" : 2.54 * mm});
        }
    });
